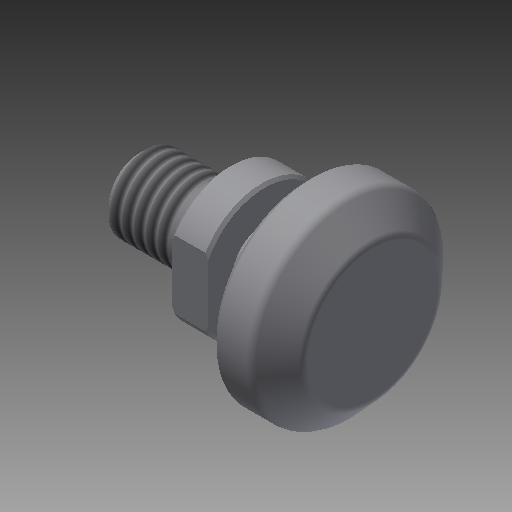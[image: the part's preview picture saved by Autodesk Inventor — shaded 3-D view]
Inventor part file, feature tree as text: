
AUTODESK INVENTOR PART (.ipt)
format: ipt  version: 2018 (Build 220112000, 112)  size: 189,952 bytes
history: native  units: mm
features: other x14, sketch x3, extrude x2, revolve x1, thread x1
ambient origin geometry x8: Origin, YZ Plane, XZ Plane, XY Plane, X Axis, Y Axis, Z Axis, Center Point
bodies: Solid1 (feature_tree)
feature tree (21):
  revolve  "Revolution1"  [1 undecoded]
  thread  "Thread1"  [1 undecoded]
  extrude  "Extrusion1"  [1 undecoded]
  extrude  "Extrusion2"  [1 undecoded]
  other  "side_1_XY"
  other  "side_1_YZ"
  other  "side_1_ZX"
  other  "side_1_X"
  other  "side_1_Y"
  other  "side_1_Z"
  other  "side_1_Center"
  other  "side_2_XY"
  other  "side_2_YZ"
  other  "side_2_ZX"
  other  "side_2_X"
  other  "side_2_Y"
  other  "side_2_Z"
  other  "side_2_Center"
  sketch  "Skizze_1"  dims[d0=360.0deg d1=6.233mm d2=0.0mm d3=10.0mm d4=0.0mm]
  sketch  "Skizze_2"  dims[d5=10.0mm d6=0.0mm]
  sketch  "Skizze_3"
note: 4 required parameter values undecoded (feature->parameter linkage not recoverable at this tier; creation-order binding heuristic only, values carry confidence <= 0.55)